FREECAD ASSEMBLY — COMPONENT RECIPES ("Assembly")

This assembly document has 6 components, labeled P0..P5 below (a component is one placed body or linked part). 0 of them carry a construction recipe — the FreeCAD feature program that regenerates the part from scratch, quoted from this document or its linked companion documents; the rest are supplied as boundary geometry only. No exploded tour is included for this assembly.
COMPONENT P0 — geometry summary ("Anchor Rod"; no construction recipe available for this part):
  bounding box: 30.0 x 8.0 x 7.1 mm
  tessellated surface: 248 triangles
  volume: 407278519202450215710727576891715295803042737059684231015760765206776203126147692671633669854483972096 mm^3 (23739516884639061703043530857387527280565935318915923459026861499177247595466301667311331699874332672% of its bounding box)
COMPONENT P1 — geometry summary ("Bearing"; no construction recipe available for this part):
  bounding box: 22.0 x 19.1 x 7.0 mm
  tessellated surface: 732 triangles
  volume: 19191532014900856796002533233474203247228993258203042702615044375600994847183415017472 mm^3 (654087140841342806264228651130530872014381321263494486477904553161721090544075014144% of its bounding box)
  symmetry: 2-fold rotationally symmetric about the x axis; 2-fold rotationally symmetric about the y axis; 3-fold rotationally symmetric about the z axis; mirror-symmetric across its x mid-plane
COMPONENT P2 — geometry summary ("Motor"; no construction recipe available for this part):
  bounding box: 58.3 x 43.3 x 42.4 mm
  tessellated surface: 2,308 triangles
  volume: 543089001160095384866587145848895869116499751685433987879608620615435391852175200878185544679021346816 mm^3 (506813168757649819646880877148517097888432377072187783088763228129989083467919420875610309787648000% of its bounding box)
  symmetry: mirror-symmetric across its x mid-plane
COMPONENT P3 — geometry summary ("Pulley"; no construction recipe available for this part):
  bounding box: 41.2 x 40.8 x 18.0 mm
  tessellated surface: 6,332 triangles
  volume: 25405709530533303423304747310514640625468591710080502038144461787265666864229214928912365697466630144 mm^3 (84067470518586692755407192308667452739144430146496997141664317342601841532152746201276568710414336% of its bounding box)
COMPONENT P4 — geometry summary ("Shaft"; no construction recipe available for this part):
  bounding box: 80.0 x 8.0 x 7.1 mm
  tessellated surface: 600 triangles
  volume: 1068541775478241696430420140391203855160751852056720047470795660198841225613295542220284529310496194560 mm^3 (23356251611227232610299633841305915172428046705160977438971820988375023079719665777987612221072474112% of its bounding box)
COMPONENT P5 — geometry summary ("Threaded Rod"; no construction recipe available for this part):
  bounding box: 150.0 x 10.0 x 10.0 mm
  tessellated surface: 880 triangles
  volume: 15028247824636888278844496427694274168516468634921930240357939834857510096964224814373819866756939776 mm^3 (100188318830912585692571175022106932699227843448514462748876291948013265487535067893256716520783872% of its bounding box)
PROVENANCE & LICENSES
A FreeCAD (.FCStd) document from a public repository crawl; recipes are the document's own serialized feature recipes (and, for linked parts, companion documents' recipes).
License: as declared in the source repository (recorded in the dataset sidecar).
